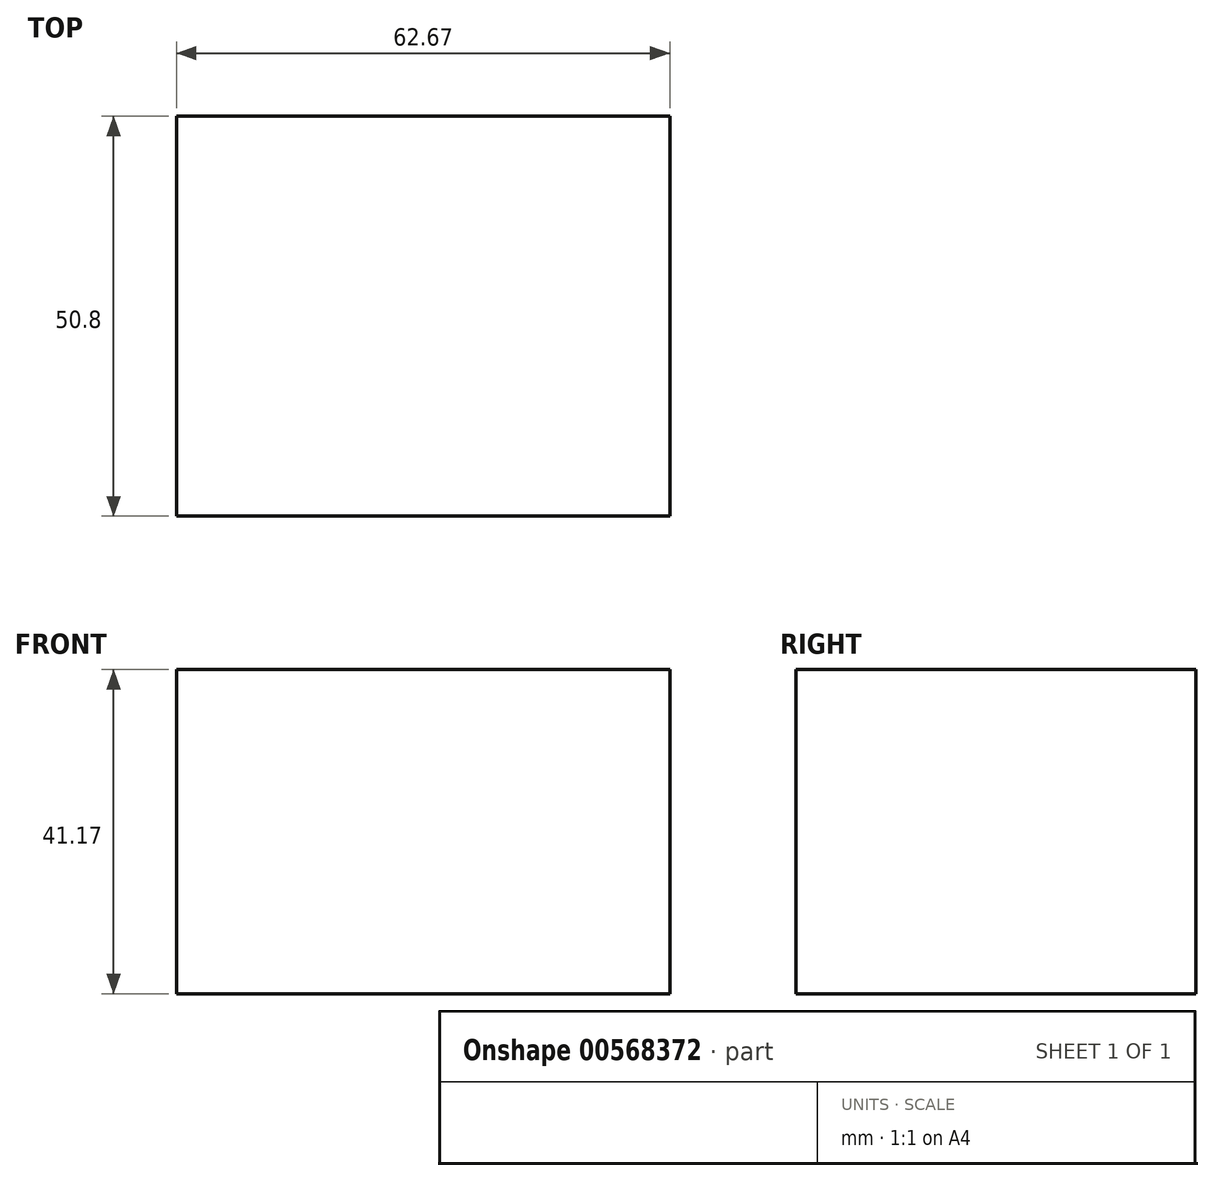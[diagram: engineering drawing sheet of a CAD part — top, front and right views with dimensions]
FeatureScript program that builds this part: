
annotation { "Feature Type Name" : "Feature", "Feature Type Description" : "" }
export const myFeature = defineFeature(function(context is Context, id is Id, definition is map)
    precondition{}
    {
        {
            var Q0;
            Q0=qCreatedBy(makeId("Front.planeOp"),FACE);
            var sketch = newSketch(context, id + "F0", { "sketchPlane" : qUnion([Q0])});
            skLineSegment(sketch, "E0.bottom", {"start": v(-27.99, -17.34) * mm, "end": v(34.68, -17.34) * mm});
            skLineSegment(sketch, "E0.top", {"start": v(-27.99, 23.83) * mm, "end": v(34.68, 23.83) * mm});
            skLineSegment(sketch, "E0.left", {"start": v(-27.99, -17.34) * mm, "end": v(-27.99, 23.83) * mm});
            skLineSegment(sketch, "E0.right", {"start": v(34.68, -17.34) * mm, "end": v(34.68, 23.83) * mm});
            skLineSegment(sketch, "E1", {"start": v(-27.99, -17.34) * mm, "end": v(34.68, 23.83) * mm, "construction": true});
            skSolve(sketch);
        }
        {
            var Q0;
            Q0 = qSketchRegion(id + "F0", true);
            extrude(context, id + "F1", {"entities" : qUnion([Q0]), "depth" : 50.8 * mm, "offsetDistance" : 25.4 * mm});
        }
    });
